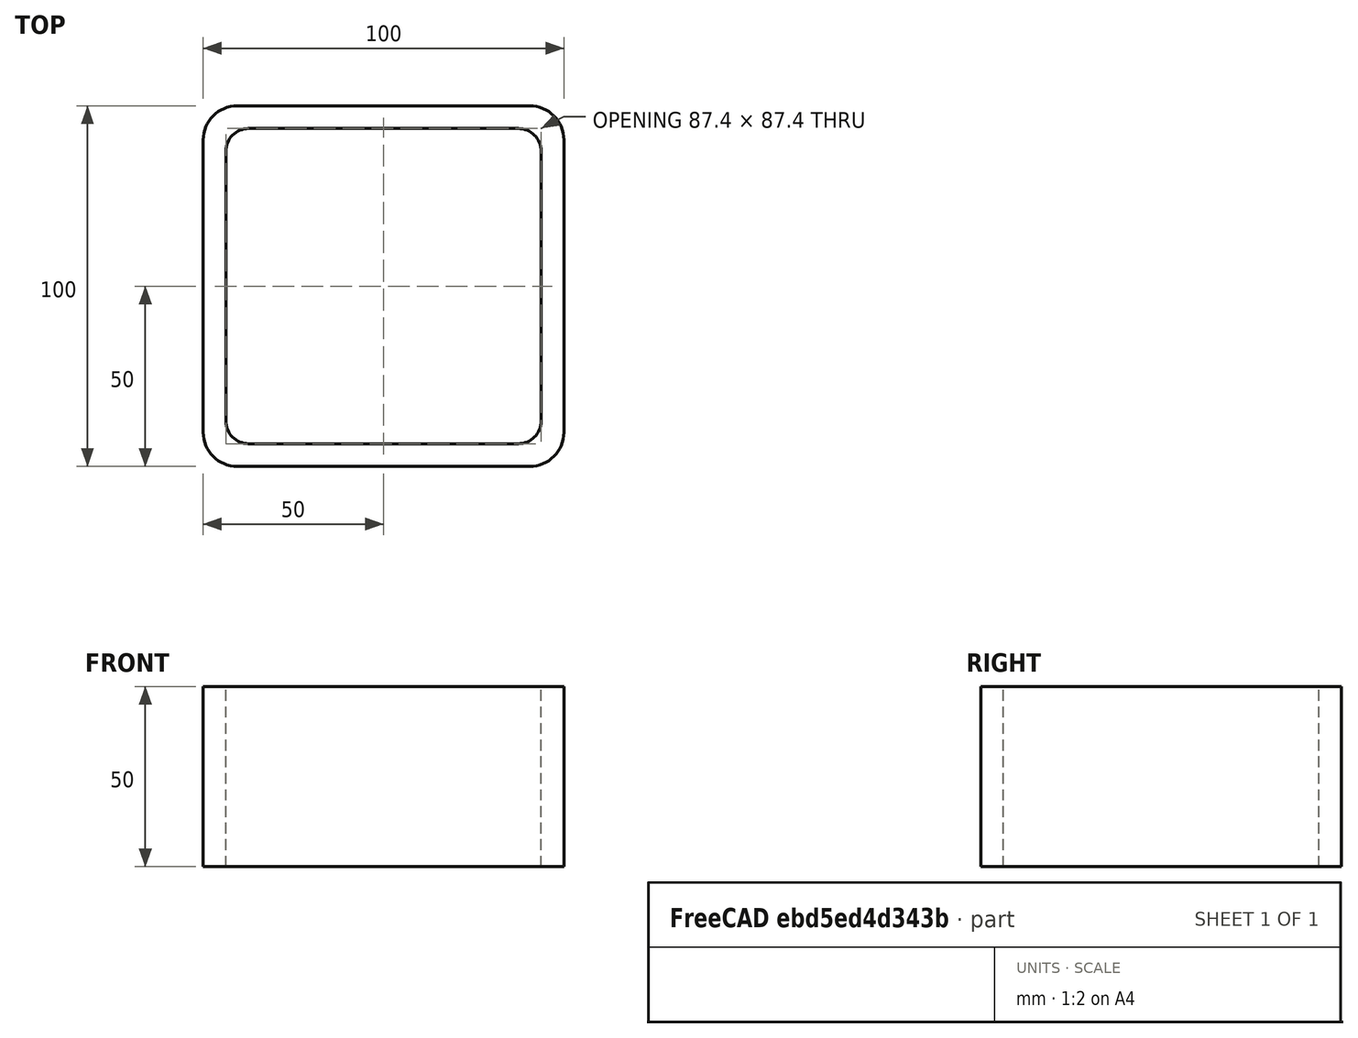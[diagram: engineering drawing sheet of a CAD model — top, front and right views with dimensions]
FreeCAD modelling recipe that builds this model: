
FCSTD DOCUMENT  (FreeCAD 0.15R4671 (Git))
Label: Square hollow section 100x100x6.3 EN10219 S235JRH
License: All rights reserved
LicenseURL: http://en.wikipedia.org/wiki/All_rights_reserved
objects: Sketcher::SketchObject×1, Part::Extrusion×1
note: 2 computed .brp shape members not serialized (recipe doc carries the construction recipe); baked Part::Feature solids carry a one-line shape summary decoded from their .brp

FEATURE [Sketcher::SketchObject] Sketch
  sketch-geometry (16):
    g0: LineSegment StartX=-37.4 StartY=43.7 StartZ=0 EndX=37.4 EndY=43.7 EndZ=0
    g1: LineSegment StartX=43.7 StartY=37.4 StartZ=0 EndX=43.7 EndY=-37.4 EndZ=0
    g2: LineSegment StartX=37.4 StartY=-43.7 StartZ=0 EndX=-37.4 EndY=-43.7 EndZ=0
    g3: LineSegment StartX=-43.7 StartY=-37.4 StartZ=0 EndX=-43.7 EndY=37.4 EndZ=0
    g4: LineSegment StartX=-40.55 StartY=50 StartZ=0 EndX=40.55 EndY=50 EndZ=0
    g5: LineSegment StartX=50 StartY=40.55 StartZ=0 EndX=50 EndY=-40.55 EndZ=0
    g6: LineSegment StartX=40.55 StartY=-50 StartZ=0 EndX=-40.55 EndY=-50 EndZ=0
    g7: LineSegment StartX=-50 StartY=-40.55 StartZ=0 EndX=-50 EndY=40.55 EndZ=0
    g8: ArcOfCircle CenterX=-37.4 CenterY=37.4 CenterZ=0 NormalX=0 NormalY=0 NormalZ=1 Radius=6.3 StartAngle=1.5708 EndAngle=3.14159
    g9: ArcOfCircle CenterX=37.4 CenterY=37.4 CenterZ=0 NormalX=0 NormalY=0 NormalZ=1 Radius=6.3 StartAngle=0 EndAngle=1.5708
    g10: ArcOfCircle CenterX=37.4 CenterY=-37.4 CenterZ=0 NormalX=0 NormalY=0 NormalZ=1 Radius=6.3 StartAngle=4.71239 EndAngle=6.28319
    g11: ArcOfCircle CenterX=-37.4 CenterY=-37.4 CenterZ=0 NormalX=0 NormalY=0 NormalZ=1 Radius=6.3 StartAngle=3.14159 EndAngle=4.71239
    g12: ArcOfCircle CenterX=40.55 CenterY=40.55 CenterZ=0 NormalX=0 NormalY=0 NormalZ=1 Radius=9.45 StartAngle=0 EndAngle=1.5708
    g13: ArcOfCircle CenterX=40.55 CenterY=-40.55 CenterZ=0 NormalX=0 NormalY=0 NormalZ=1 Radius=9.45 StartAngle=4.71239 EndAngle=6.28319
    g14: ArcOfCircle CenterX=-40.55 CenterY=-40.55 CenterZ=0 NormalX=0 NormalY=0 NormalZ=1 Radius=9.45 StartAngle=3.14159 EndAngle=4.71239
    g15: ArcOfCircle CenterX=-40.55 CenterY=40.55 CenterZ=0 NormalX=0 NormalY=0 NormalZ=1 Radius=9.45 StartAngle=1.5708 EndAngle=3.14159
  constraints (36):
    c: Horizontal(g2)
    c: Vertical(g3)
    c: Horizontal(g6)
    c: Vertical(g7)
    c: Tangent(g3,g8) = 1.5708
    c: Tangent(g0,g8) = 1.5708
    c: Tangent(g0,g9) = 1.5708
    c: Tangent(g1,g9) = 1.5708
    c: Tangent(g1,g10) = 1.5708
    c: Tangent(g2,g10) = 1.5708
    c: Tangent(g2,g11) = 1.5708
    c: Tangent(g3,g11) = 1.5708
    c: Tangent(g4,g12) = 1.5708
    c: Tangent(g5,g12) = 1.5708
    c: Tangent(g5,g13) = 1.5708
    c: Tangent(g6,g13) = 1.5708
    c: Tangent(g6,g14) = 1.5708
    c: Tangent(g7,g14) = 1.5708
    c: Tangent(g7,g15) = 1.5708
    c: Tangent(g4,g15) = 1.5708
    c: Equal(g9,g8)
    c: Equal(g9,g11)
    c: Equal(g9,g10)
    c: Equal(g12,g15)
    c: Equal(g12,g14)
    c: Equal(g12,g13)
    c: Symmetric(g4,g6,g-1)
    c: Symmetric(g7,g5,g-2)
    c: DistanceY(g4,g6) = -100
    c: DistanceX(g7,g5) = 100
    c: Symmetric(g3,g1,g-2)
    c: Symmetric(g0,g2,g-1)
    c: DistanceY(g0,g4) = 6.3
    c: DistanceX(g5,g1) = -6.3
    c: Radius(g9) = 6.3
    c: Radius(g12) = 9.45
FEATURE [Part::Extrusion] Extrude  label="Square hollow section 100x100x6.3 EN10219 S235JRH"
  Base = -> Sketch
  Dir = (0,0,50)
  Solid = true
